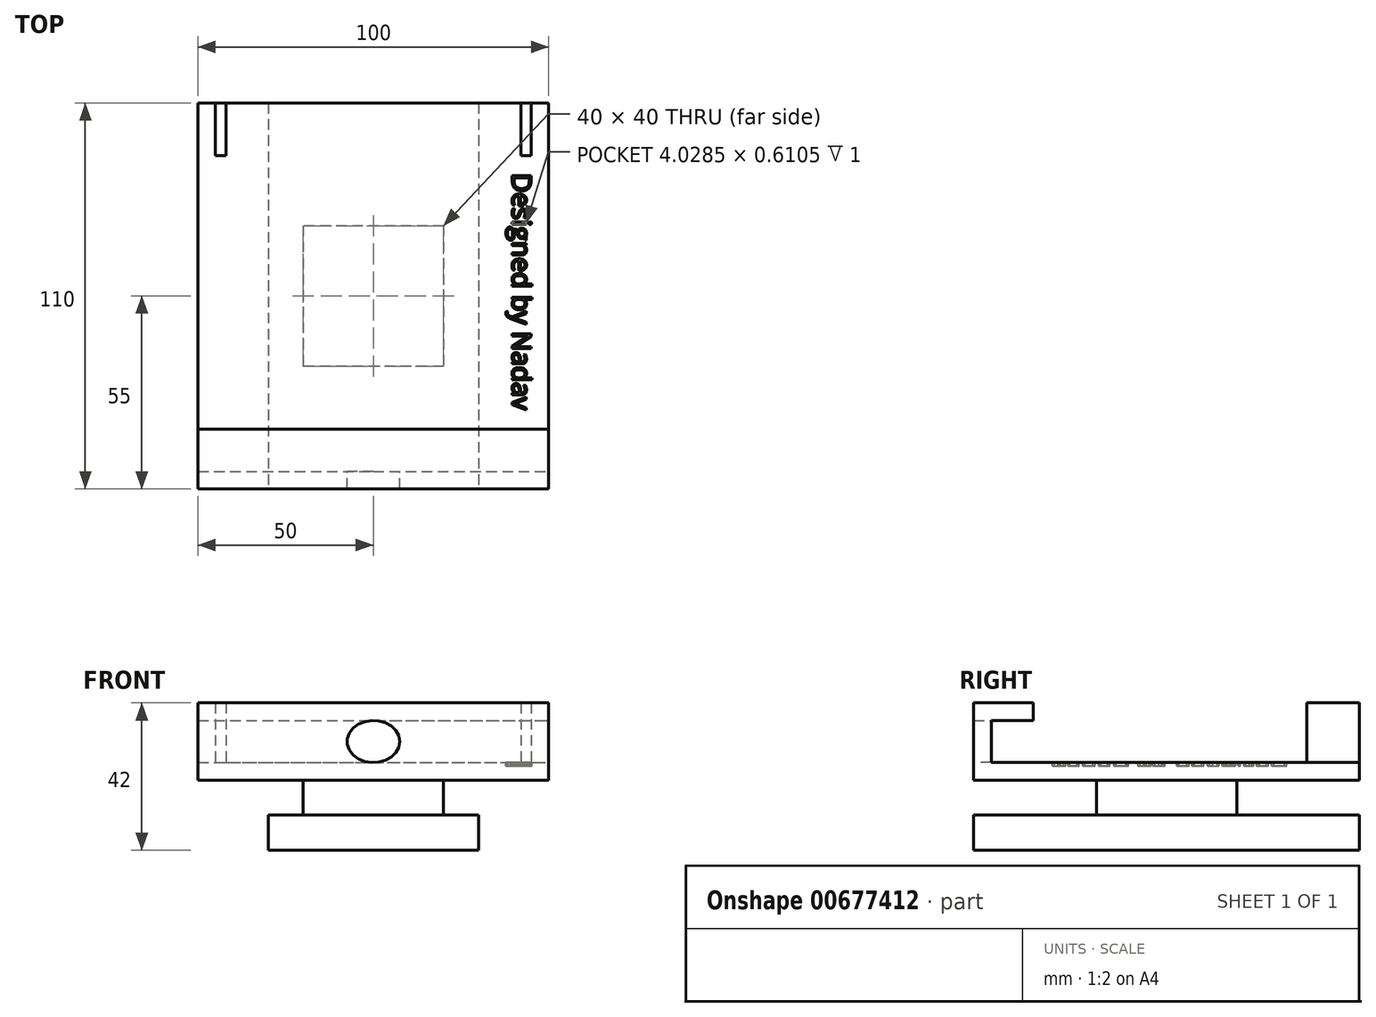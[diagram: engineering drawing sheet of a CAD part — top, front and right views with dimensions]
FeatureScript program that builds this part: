
annotation { "Feature Type Name" : "Feature", "Feature Type Description" : "" }
export const myFeature = defineFeature(function(context is Context, id is Id, definition is map)
    precondition{}
    {
        {
            var Q0;
            Q0=qCreatedBy(makeId("Top.planeOp"),FACE);
            var sketch = newSketch(context, id + "F0", { "sketchPlane" : qUnion([Q0])});
            skLineSegment(sketch, "E0.bottom", {"start": v(30, 55) * mm, "end": v(-30, 55) * mm});
            skLineSegment(sketch, "E0.top", {"start": v(30, -55) * mm, "end": v(-30, -55) * mm});
            skLineSegment(sketch, "E0.left", {"start": v(30, 55) * mm, "end": v(30, -55) * mm});
            skLineSegment(sketch, "E0.right", {"start": v(-30, 55) * mm, "end": v(-30, -55) * mm});
            skPoint(sketch, "E0.middle", {"position": v(0, 0) * mm});
            skPoint(sketch, "E1", {"position": v(0, -55) * mm});
            skSolve(sketch);
        }
        {
            var Q0;
            Q0=makeQuery(id+"F0.imprint","IMPRINT",FACE,{"disambiguationData":[TD([[makeQuery(id+"F0.imprint","IMPRINT",EDGE,{"derivedFrom":sQuery(id+"F0.wireOp",EDGE,"E0.bottom")}),1.0]])]});
            extrude(context, id + "F1", {"entities" : qUnion([Q0]), "depth" : 10 * mm, "offsetDistance" : 25 * mm});
        }
        {
            var Q0;
            Q0=makeQuery(id+"F1.opExtrude","CAP_FACE",FACE,{"disambiguationData":[OSD([sQuery(id+"F0.wireOp",EDGE,"E0.bottom"),sQuery(id+"F0.wireOp",EDGE,"E0.top"),sQuery(id+"F0.wireOp",EDGE,"E0.left"),sQuery(id+"F0.wireOp",EDGE,"E0.right")])],"isStart":false});
            var sketch = newSketch(context, id + "F2", { "sketchPlane" : qUnion([Q0])});
            skLineSegment(sketch, "E2.bottom", {"start": v(20, 20) * mm, "end": v(-20, 20) * mm});
            skLineSegment(sketch, "E2.top", {"start": v(20, -20) * mm, "end": v(-20, -20) * mm});
            skLineSegment(sketch, "E2.left", {"start": v(20, 20) * mm, "end": v(20, -20) * mm});
            skLineSegment(sketch, "E2.right", {"start": v(-20, 20) * mm, "end": v(-20, -20) * mm});
            skPoint(sketch, "E2.middle", {"position": v(0, 0) * mm});
            skSolve(sketch);
        }
        {
            var Q0;
            Q0=makeQuery(id+"F2.imprint","IMPRINT",FACE,{"disambiguationData":[TD([[makeQuery(id+"F2.imprint","IMPRINT",EDGE,{"derivedFrom":sQuery(id+"F2.wireOp",EDGE,"E2.bottom")}),1.0]])]});
            extrude(context, id + "F3", {"entities" : qUnion([Q0]), "operationType" : NewBodyOperationType.ADD, "depth" : 10 * mm, "offsetDistance" : 25 * mm});
        }
        {
            var Q0;
            Q0=makeQuery(id+"F3.opExtrude","CAP_FACE",FACE,{"disambiguationData":[OSD([sQuery(id+"F2.wireOp",EDGE,"E2.bottom"),sQuery(id+"F2.wireOp",EDGE,"E2.top"),sQuery(id+"F2.wireOp",EDGE,"E2.left"),sQuery(id+"F2.wireOp",EDGE,"E2.right")])],"isStart":false});
            var sketch = newSketch(context, id + "F4", { "sketchPlane" : qUnion([Q0])});
            skLineSegment(sketch, "E3.bottom", {"start": v(-50, 55) * mm, "end": v(50, 55) * mm});
            skLineSegment(sketch, "E3.top", {"start": v(-50, -55) * mm, "end": v(50, -55) * mm});
            skLineSegment(sketch, "E3.left", {"start": v(-50, 55) * mm, "end": v(-50, -55) * mm});
            skLineSegment(sketch, "E3.right", {"start": v(50, 55) * mm, "end": v(50, -55) * mm});
            skPoint(sketch, "E4", {"position": v(0, -55) * mm});
            skLineSegment(sketch, "E5", {"start": v(0, 0) * mm, "end": v(0, -55) * mm, "construction": true});
            skSolve(sketch);
        }
        {
            var Q0;
            Q0=makeQuery(id+"F4.imprint","IMPRINT",FACE,{"disambiguationData":[TD([[makeQuery(id+"F4.imprint","IMPRINT",EDGE,{"derivedFrom":sQuery(id+"F4.wireOp",EDGE,"E3.top")}),1.0]])]});
            var Q1;
            {var subQ5=makeQuery(id+"F3.opExtrude","CAP_EDGE",EDGE,{"disambiguationData":[OSD([sQuery(id+"F2.wireOp",EDGE,"E2.top")])],"isStart":false});Q1=makeQuery(id+"F4.imprint","IMPRINT",FACE,{"disambiguationData":[TD([[makeQuery(id+"F4.imprint","IMPRINT",EDGE,{"derivedFrom":subQ5}),-1.0]])]});}
            extrude(context, id + "F5", {"entities" : qUnion([Q0, Q1]), "operationType" : NewBodyOperationType.ADD, "depth" : 5 * mm, "offsetDistance" : 25 * mm});
        }
        {
            var Q0;
            Q0=makeQuery(id+"F5.opExtrude","CAP_FACE",FACE,{"disambiguationData":[OSD([sQuery(id+"F4.wireOp",EDGE,"E3.bottom"),sQuery(id+"F4.wireOp",EDGE,"E3.top"),sQuery(id+"F4.wireOp",EDGE,"E3.left"),sQuery(id+"F4.wireOp",EDGE,"E3.right")])],"isStart":false});
            var sketch = newSketch(context, id + "F6", { "sketchPlane" : qUnion([Q0])});
            skLineSegment(sketch, "E6.bottom", {"start": v(-50, -50) * mm, "end": v(50, -50) * mm});
            skLineSegment(sketch, "E6.top", {"start": v(-50, -55) * mm, "end": v(50, -55) * mm});
            skLineSegment(sketch, "E6.left", {"start": v(-50, -50) * mm, "end": v(-50, -55) * mm});
            skLineSegment(sketch, "E6.right", {"start": v(50, -50) * mm, "end": v(50, -55) * mm});
            skLineSegment(sketch, "E7.bottom", {"start": v(-45, 55) * mm, "end": v(-42, 55) * mm});
            skLineSegment(sketch, "E7.top", {"start": v(-45, 40) * mm, "end": v(-42, 40) * mm});
            skLineSegment(sketch, "E7.left", {"start": v(-42, 55) * mm, "end": v(-42, 40) * mm});
            skLineSegment(sketch, "E7.right", {"start": v(-45, 55) * mm, "end": v(-45, 40) * mm});
            skLineSegment(sketch, "E8.bottom", {"start": v(42, 55) * mm, "end": v(45, 55) * mm});
            skLineSegment(sketch, "E8.top", {"start": v(42, 40) * mm, "end": v(45, 40) * mm});
            skLineSegment(sketch, "E8.left", {"start": v(45, 55) * mm, "end": v(45, 40) * mm});
            skLineSegment(sketch, "E8.right", {"start": v(42, 55) * mm, "end": v(42, 40) * mm});
            skLineSegment(sketch, "E9", {"start": v(-29.54, 40) * mm, "end": v(-29.54, -50) * mm, "construction": true});
            skLineSegment(sketch, "E10", {"start": v(-45, 40) * mm, "end": v(45, 40) * mm, "construction": true});
            skSolve(sketch);
        }
        {
            var Q0;
            Q0=makeQuery(id+"F6.imprint","IMPRINT",FACE,{"disambiguationData":[TD([[makeQuery(id+"F6.imprint","IMPRINT",EDGE,{"derivedFrom":sQuery(id+"F6.wireOp",EDGE,"E7.bottom")}),-1.0]])]});
            var Q1;
            Q1=makeQuery(id+"F6.imprint","IMPRINT",FACE,{"disambiguationData":[TD([[makeQuery(id+"F6.imprint","IMPRINT",EDGE,{"derivedFrom":sQuery(id+"F6.wireOp",EDGE,"E8.bottom")}),-1.0]])]});
            var Q2;
            Q2=makeQuery(id+"F6.imprint","IMPRINT",FACE,{"disambiguationData":[TD([[makeQuery(id+"F6.imprint","IMPRINT",EDGE,{"derivedFrom":sQuery(id+"F6.wireOp",EDGE,"E6.bottom")}),-1.0]])]});
            extrude(context, id + "F7", {"entities" : qUnion([Q0, Q1, Q2]), "operationType" : NewBodyOperationType.ADD, "depth" : 17 * mm, "offsetDistance" : 25 * mm});
        }
        {
            var Q0;
            Q0=makeQuery(id+"F7.opExtrude","SWEPT_FACE",FACE,{"disambiguationData":[OSD([sQuery(id+"F6.wireOp",EDGE,"E6.bottom")])]});
            var sketch = newSketch(context, id + "F8", { "sketchPlane" : qUnion([Q0])});
            skLineSegment(sketch, "E11.bottom", {"start": v(50, 37) * mm, "end": v(-50, 37) * mm});
            skLineSegment(sketch, "E11.top", {"start": v(50, 42) * mm, "end": v(-50, 42) * mm});
            skLineSegment(sketch, "E11.left", {"start": v(50, 37) * mm, "end": v(50, 42) * mm});
            skLineSegment(sketch, "E11.right", {"start": v(-50, 37) * mm, "end": v(-50, 42) * mm});
            skLineSegment(sketch, "E12", {"start": v(0, 25) * mm, "end": v(0, 37) * mm, "construction": true});
            skPoint(sketch, "E13", {"position": v(0, 31) * mm});
            skEllipse(sketch, "E14", {"center": v(0, 31) * mm, "majorRadius": 7.5 * mm, "minorRadius": 6 * mm, "majorAxis": v(-1, 0)});
            skLineSegment(sketch, "E15", {"start": v(-7.5, 25) * mm, "end": v(-7.5, 37) * mm, "construction": true});
            skLineSegment(sketch, "E16", {"start": v(7.5, 25) * mm, "end": v(7.5, 37) * mm, "construction": true});
            skPoint(sketch, "E16.endSnap0", {"position": v(7.5, 31) * mm});
            skSolve(sketch);
        }
        {
            var Q0;
            Q0=makeQuery(id+"F8.imprint","IMPRINT",FACE,{"disambiguationData":[TD([[makeQuery(id+"F8.imprint","IMPRINT",EDGE,{"derivedFrom":sQuery(id+"F8.wireOp",EDGE,"E11.bottom")}),-1.0]])]});
            extrude(context, id + "F9", {"entities" : qUnion([Q0]), "operationType" : NewBodyOperationType.ADD, "depth" : 12 * mm, "offsetDistance" : 25 * mm});
        }
        {
            var Q0;
            {var subQ0=sQuery(id+"F8.wireOp",EDGE,"E14");var subQ1=makeQuery(id+"F8.imprint","INTERSECT",VERTEX,{"derivedFrom":[sQuery(id+"F8.wireOp",EDGE,"E11.bottom"),subQ0]});Q0=makeQuery(id+"F8.imprint","IMPRINT",FACE,{"disambiguationData":[TD([[makeQuery(id+"F8.imprint","IMPRINT",EDGE,{"disambiguationData":[TD([[subQ1,1.0]])],"derivedFrom":subQ0}),1.0]])]});}
            extrude(context, id + "F10", {"entities" : qUnion([Q0]), "operationType" : NewBodyOperationType.REMOVE, "oppositeDirection" : true, "depth" : 25 * mm, "offsetDistance" : 25 * mm});
        }
        {
            var Q0;
            Q0=makeQuery(id+"F5.opExtrude","CAP_FACE",FACE,{"disambiguationData":[OSD([sQuery(id+"F4.wireOp",EDGE,"E3.bottom"),sQuery(id+"F4.wireOp",EDGE,"E3.top"),sQuery(id+"F4.wireOp",EDGE,"E3.left"),sQuery(id+"F4.wireOp",EDGE,"E3.right")])],"isStart":false});
            var sketch = newSketch(context, id + "F11", { "sketchPlane" : qUnion([Q0])});
            skText(sketch, "E17", { "text": "Designed by Nadav", "fontName": "OpenSans-Regular.ttf"});
            const initialGuessF11  = {"E17": [0.03958, 0.035, 0, -1, 0.00542]};
            skSetInitialGuess(sketch, initialGuessF11);
            skSolve(sketch);
        }
        {
            var Q0;
            Q0 = qSketchRegion(id + "F11", true);
            extrude(context, id + "F12", {"entities" : qUnion([Q0]), "operationType" : NewBodyOperationType.REMOVE, "oppositeDirection" : true, "depth" : 1 * mm, "offsetDistance" : 25 * mm});
        }
    });
